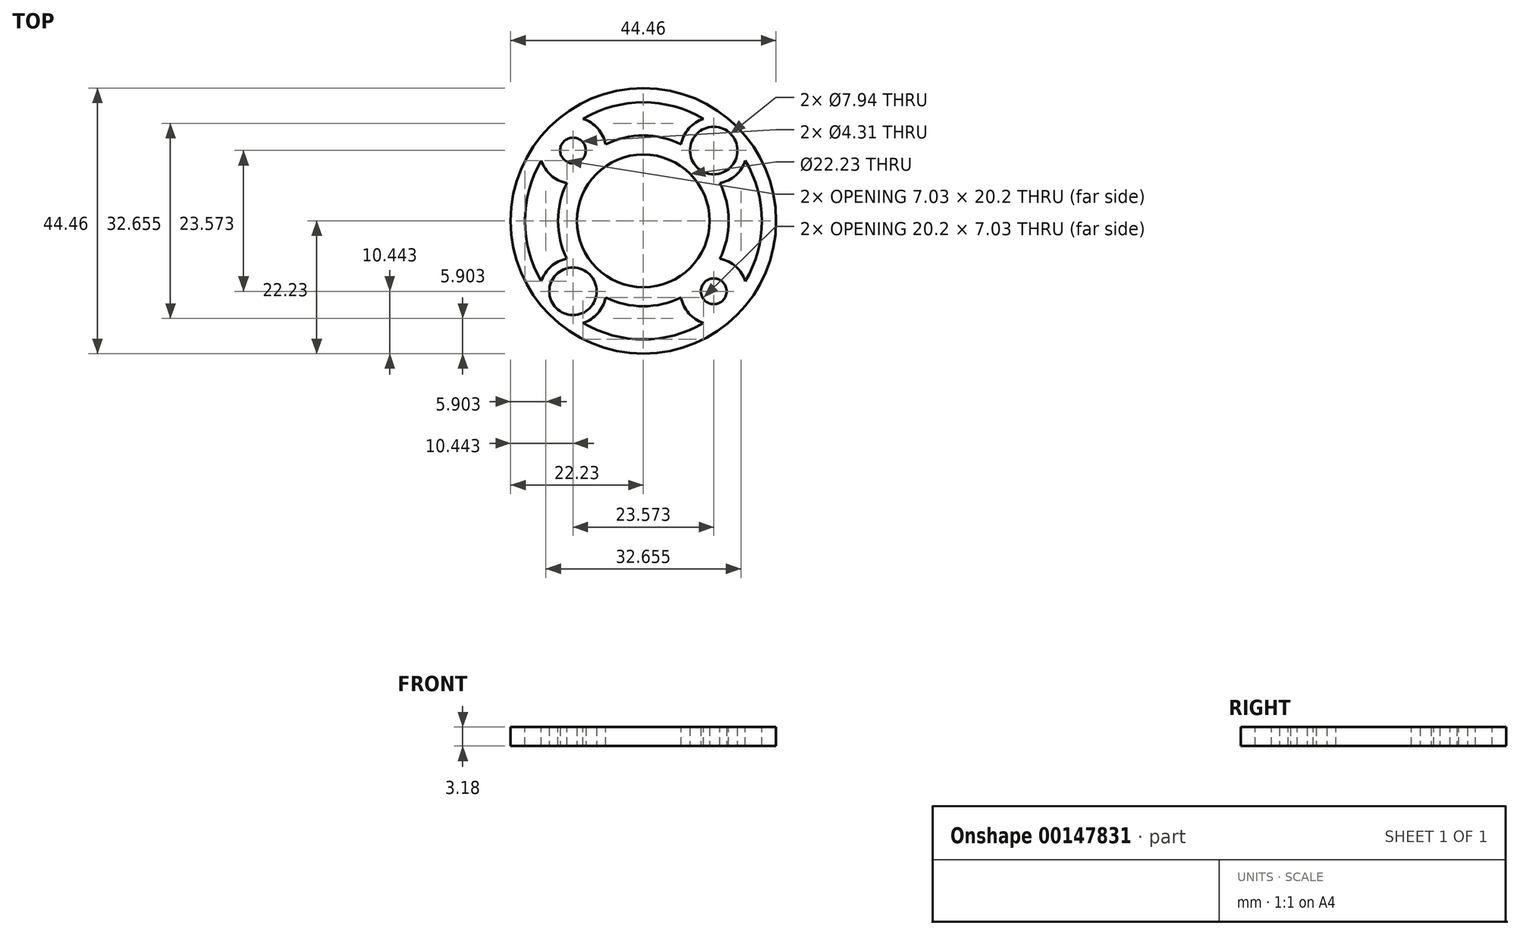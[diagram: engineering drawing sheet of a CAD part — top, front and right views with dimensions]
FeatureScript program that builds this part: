
annotation { "Feature Type Name" : "Feature", "Feature Type Description" : "" }
export const myFeature = defineFeature(function(context is Context, id is Id, definition is map)
    precondition{}
    {
        {
            var Q0;
            Q0=qCreatedBy(makeId("Top.planeOp"),FACE);
            var sketch = newSketch(context, id + "F0", { "sketchPlane" : qUnion([Q0])});
            skCircle(sketch, "E0", {"center": v(0, 0) * mm, "radius": 22.23 * mm});
            skCircle(sketch, "E1", {"center": v(0, 0) * mm, "radius": 11.11 * mm});
            skLineSegment(sketch, "E2.bottom", {"start": v(-11.79, 11.79) * mm, "end": v(11.79, 11.79) * mm, "construction": true});
            skLineSegment(sketch, "E2.top", {"start": v(-11.79, -11.79) * mm, "end": v(11.79, -11.79) * mm, "construction": true});
            skLineSegment(sketch, "E2.left", {"start": v(-11.79, 11.79) * mm, "end": v(-11.79, -11.79) * mm, "construction": true});
            skLineSegment(sketch, "E2.right", {"start": v(11.79, 11.79) * mm, "end": v(11.79, -11.79) * mm, "construction": true});
            skCircle(sketch, "E3", {"center": v(11.79, 11.79) * mm, "radius": 3.97 * mm});
            skCircle(sketch, "E4", {"center": v(-11.79, 11.79) * mm, "radius": 2.15 * mm});
            skCircle(sketch, "E5", {"center": v(-11.79, -11.79) * mm, "radius": 3.97 * mm});
            skCircle(sketch, "E6", {"center": v(11.79, -11.79) * mm, "radius": 2.15 * mm});
            skCircle(sketch, "E7", {"center": v(11.79, 11.79) * mm, "radius": 5.56 * mm, "construction": true});
            skSolve(sketch);
        }
        {
            var Q0;
            Q0=qSketchRegion(id+"F0",true);
            extrude(context, id + "F1", {"entities" : qUnion([Q0]), "depth" : 3.17 * mm});
        }
        {
            var Q0;
            Q0=makeQuery(id+"F1.opExtrude","CAP_FACE",FACE,{"disambiguationData":[OSD([sQuery(id+"F0.wireOp",EDGE,"E0"),sQuery(id+"F0.wireOp",EDGE,"E1"),sQuery(id+"F0.wireOp",EDGE,"E3"),sQuery(id+"F0.wireOp",EDGE,"E4"),sQuery(id+"F0.wireOp",EDGE,"E5"),sQuery(id+"F0.wireOp",EDGE,"E6")])],"isStart":false});
            var sketch = newSketch(context, id + "F2", { "sketchPlane" : qUnion([Q0])});
            skArc(sketch, "E8", {"start": v(-6.33, 12.81) * mm, "mid": v(-7.62, 15.47) * mm, "end": v(-10.1, 17.08) * mm});
            skArc(sketch, "E9", {"start": v(10.1, 17.08) * mm, "mid": v(7.62, 15.47) * mm, "end": v(6.33, 12.81) * mm});
            skArc(sketch, "E10", {"start": v(6.33, 12.81) * mm, "mid": v(0, 14.29) * mm, "end": v(-6.33, 12.81) * mm});
            skArc(sketch, "E11", {"start": v(10.1, 17.08) * mm, "mid": v(0, 19.84) * mm, "end": v(-10.1, 17.08) * mm});
            skArc(sketch, "E12", {"start": v(-17.08, 10.1) * mm, "mid": v(-15.47, 7.62) * mm, "end": v(-12.81, 6.33) * mm});
            skArc(sketch, "E13", {"start": v(-12.81, 6.33) * mm, "mid": v(-14.29, 0) * mm, "end": v(-12.81, -6.33) * mm});
            skArc(sketch, "E14", {"start": v(-12.81, -6.33) * mm, "mid": v(-15.47, -7.62) * mm, "end": v(-17.08, -10.1) * mm});
            skArc(sketch, "E15", {"start": v(-17.08, 10.1) * mm, "mid": v(-19.84, 0) * mm, "end": v(-17.08, -10.1) * mm});
            skArc(sketch, "E16", {"start": v(12.81, 6.33) * mm, "mid": v(15.47, 7.62) * mm, "end": v(17.08, 10.1) * mm});
            skArc(sketch, "E17", {"start": v(17.08, -10.1) * mm, "mid": v(19.84, 0) * mm, "end": v(17.08, 10.1) * mm});
            skArc(sketch, "E18", {"start": v(12.81, -6.33) * mm, "mid": v(14.29, 0) * mm, "end": v(12.81, 6.33) * mm});
            skArc(sketch, "E19", {"start": v(17.08, -10.1) * mm, "mid": v(15.47, -7.62) * mm, "end": v(12.81, -6.33) * mm});
            skArc(sketch, "E20", {"start": v(-10.1, -17.08) * mm, "mid": v(-7.62, -15.47) * mm, "end": v(-6.33, -12.81) * mm});
            skArc(sketch, "E21", {"start": v(6.33, -12.81) * mm, "mid": v(7.62, -15.47) * mm, "end": v(10.1, -17.08) * mm});
            skArc(sketch, "E22", {"start": v(-6.33, -12.81) * mm, "mid": v(0, -14.29) * mm, "end": v(6.33, -12.81) * mm});
            skArc(sketch, "E23", {"start": v(-10.1, -17.08) * mm, "mid": v(0, -19.84) * mm, "end": v(10.1, -17.08) * mm});
            skSolve(sketch);
        }
        {
            var Q0;
            Q0=qSketchRegion(id+"F2",true);
            var Q1;
            Q1=makeQuery(id+"F1.opExtrude","CAP_FACE",FACE,{"disambiguationData":[OSD([sQuery(id+"F0.wireOp",EDGE,"E0"),sQuery(id+"F0.wireOp",EDGE,"E1"),sQuery(id+"F0.wireOp",EDGE,"E3"),sQuery(id+"F0.wireOp",EDGE,"E4"),sQuery(id+"F0.wireOp",EDGE,"E5"),sQuery(id+"F0.wireOp",EDGE,"E6")])],"isStart":true});
            extrude(context, id + "F3", {"entities" : qUnion([Q0]), "operationType" : NewBodyOperationType.REMOVE, "endBound" : BoundingType.UP_TO_SURFACE, "oppositeDirection" : true, "endBoundEntityFace" : qUnion([Q1]), "depth" : 25.4 * mm});
        }
    });
